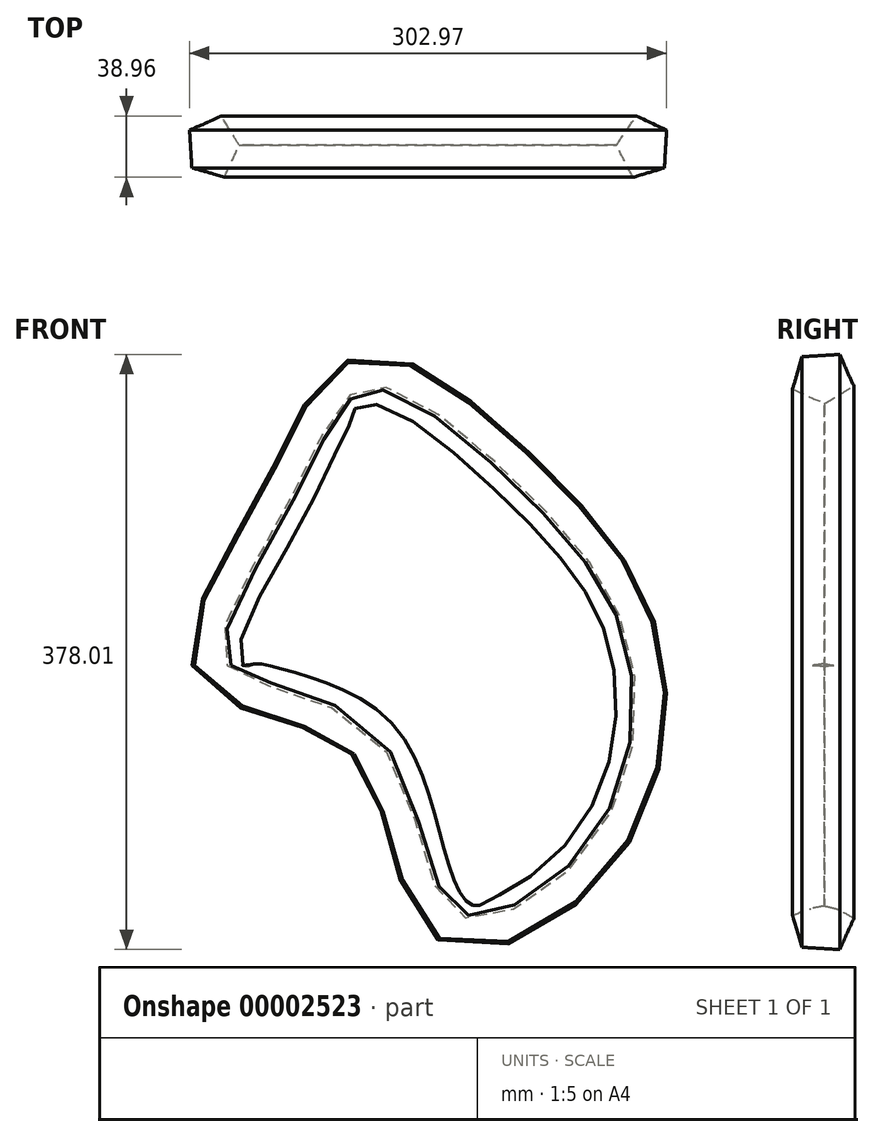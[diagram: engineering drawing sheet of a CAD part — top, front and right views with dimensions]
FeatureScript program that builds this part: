
annotation { "Feature Type Name" : "Feature", "Feature Type Description" : "" }
export const myFeature = defineFeature(function(context is Context, id is Id, definition is map)
    precondition{}
    {
        {
            var Q0;
            Q0=qCreatedBy(makeId("Top.planeOp"),FACE);
            var sketch = newSketch(context, id + "F0", { "sketchPlane" : qUnion([Q0])});
            skCircle(sketch, "E0.cCircle", {"center": v(0, 0) * mm, "radius": 16.6 * mm, "construction": true});
            skLineSegment(sketch, "E0.0", {"start": v(20.48, 1.33) * mm, "end": v(7.6, -19.07) * mm});
            skLineSegment(sketch, "E0.1", {"start": v(7.6, -19.07) * mm, "end": v(-15.8, -13.12) * mm});
            skLineSegment(sketch, "E0.2", {"start": v(-15.8, -13.12) * mm, "end": v(-17.35, 10.96) * mm});
            skLineSegment(sketch, "E0.3", {"start": v(-17.35, 10.96) * mm, "end": v(5.07, 19.9) * mm});
            skLineSegment(sketch, "E0.4", {"start": v(5.07, 19.9) * mm, "end": v(20.48, 1.33) * mm});
            skPoint(sketch, "E0.0.midPoint", {"position": v(14.04, -8.87) * mm});
            skSolve(sketch);
        }
        {
            var Q0;
            Q0=qCreatedBy(makeId("Front.planeOp"),FACE);
            var sketch = newSketch(context, id + "F1", { "sketchPlane" : qUnion([Q0])});
            skFitSpline(sketch, "E1", {"points": [v(0, 0) * mm, v(95.24, -48) * mm, v(146.36, -160.45) * mm, v(238.7, -117.77) * mm, v(263.95, 16.4) * mm, v(192.59, 118.56) * mm, v(93.94, 181.34) * mm, v(39.61, 104.4) * mm, v(0, 0) * mm]});
            skSolve(sketch);
        }
        {
            var Q0;
            Q0 = qSketchRegion(id + "F0", true);
            var Q1;
            Q1=sQuery(id+"F1.wireOp",EDGE,"E1");
            sweep(context, id + "F2", {"profiles" : qUnion([Q0]), "path" : qUnion([Q1])});
        }
    });
